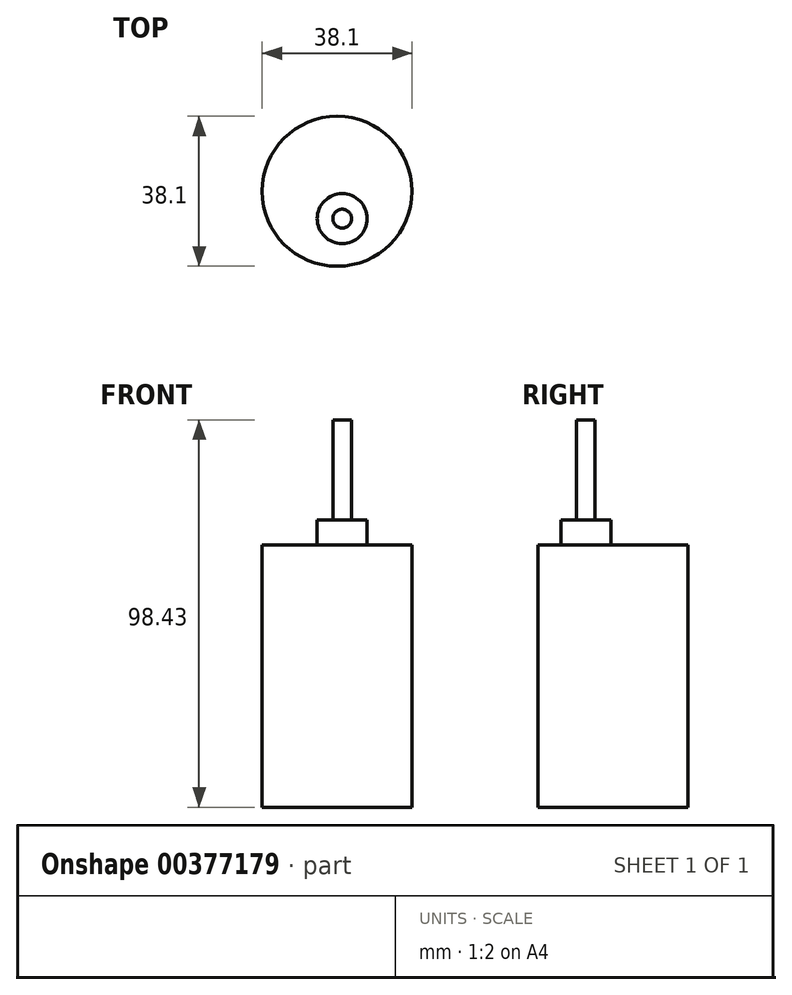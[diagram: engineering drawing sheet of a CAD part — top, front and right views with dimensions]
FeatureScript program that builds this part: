
annotation { "Feature Type Name" : "Feature", "Feature Type Description" : "" }
export const myFeature = defineFeature(function(context is Context, id is Id, definition is map)
    precondition{}
    {
        {
            var Q0;
            Q0=qCreatedBy(makeId("Top.planeOp"),FACE);
            var sketch = newSketch(context, id + "F0", { "sketchPlane" : qUnion([Q0])});
            skCircle(sketch, "E0", {"center": v(0, 0) * mm, "radius": 19.05 * mm});
            skSolve(sketch);
        }
        {
            var Q0;
            Q0 = qSketchRegion(id + "F0", true);
            extrude(context, id + "F1", {"entities" : qUnion([Q0]), "depth" : 66.67 * mm});
        }
        {
            var Q0;
            Q0=makeQuery(id+"F1.opExtrude","CAP_FACE",FACE,{"disambiguationData":[OSD([sQuery(id+"F0.wireOp",EDGE,"E0")])],"isStart":false});
            var sketch = newSketch(context, id + "F2", { "sketchPlane" : qUnion([Q0])});
            skLineSegment(sketch, "E1", {"start": v(-4.72, 18.45) * mm, "end": v(4.05, -18.61) * mm});
            skPoint(sketch, "E2", {"position": v(1.29, -6.95) * mm});
            skCircle(sketch, "E3", {"center": v(1.29, -6.95) * mm, "radius": 6.35 * mm});
            skSolve(sketch);
        }
        {
            var Q0;
            Q0 = qSketchRegion(id + "F2", true);
            extrude(context, id + "F3", {"entities" : qUnion([Q0]), "operationType" : NewBodyOperationType.ADD, "depth" : 6.35 * mm});
        }
        {
            var Q0;
            Q0=makeQuery(id+"F3.opExtrude","CAP_FACE",FACE,{"disambiguationData":[OSD([sQuery(id+"F2.wireOp",EDGE,"E3")])],"isStart":false});
            var sketch = newSketch(context, id + "F4", { "sketchPlane" : qUnion([Q0])});
            skPoint(sketch, "E4", {"position": v(1.29, -6.95) * mm});
            skCircle(sketch, "E5", {"center": v(1.29, -6.95) * mm, "radius": 2.38 * mm});
            skSolve(sketch);
        }
        {
            var Q0;
            Q0 = qSketchRegion(id + "F4", true);
            extrude(context, id + "F5", {"entities" : qUnion([Q0]), "operationType" : NewBodyOperationType.ADD, "depth" : 25.4 * mm});
        }
    });
